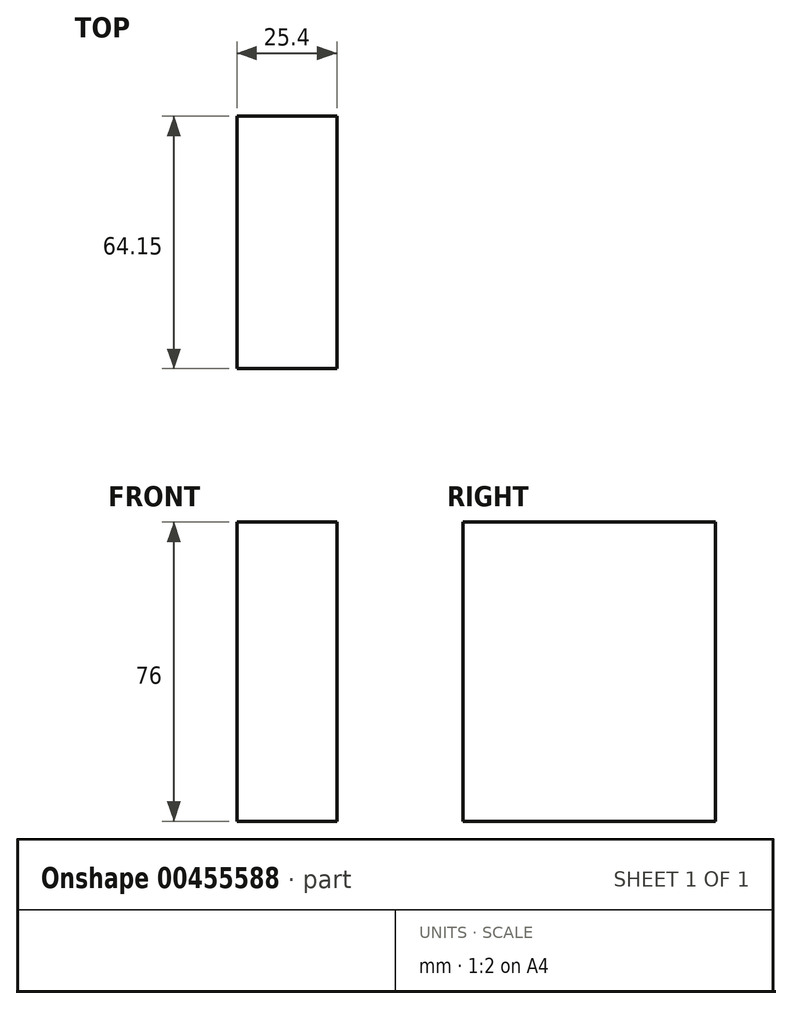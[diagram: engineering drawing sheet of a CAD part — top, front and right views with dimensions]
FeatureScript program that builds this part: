
annotation { "Feature Type Name" : "Feature", "Feature Type Description" : "" }
export const myFeature = defineFeature(function(context is Context, id is Id, definition is map)
    precondition{}
    {
        {
            var Q0;
            Q0=qCreatedBy(makeId("Right.planeOp"),FACE);
            var sketch = newSketch(context, id + "F0", { "sketchPlane" : qUnion([Q0])});
            skLineSegment(sketch, "E0.bottom", {"start": v(0, 0) * mm, "end": v(-64.15, 0) * mm});
            skLineSegment(sketch, "E0.top", {"start": v(0, 76) * mm, "end": v(-64.15, 76) * mm});
            skLineSegment(sketch, "E0.left", {"start": v(0, 0) * mm, "end": v(0, 76) * mm});
            skLineSegment(sketch, "E0.right", {"start": v(-64.15, 0) * mm, "end": v(-64.15, 76) * mm});
            skSolve(sketch);
        }
        {
            var Q0;
            Q0 = qSketchRegion(id + "F0", true);
            extrude(context, id + "F1", {"entities" : qUnion([Q0]), "depth" : 25.4 * mm});
        }
    });
